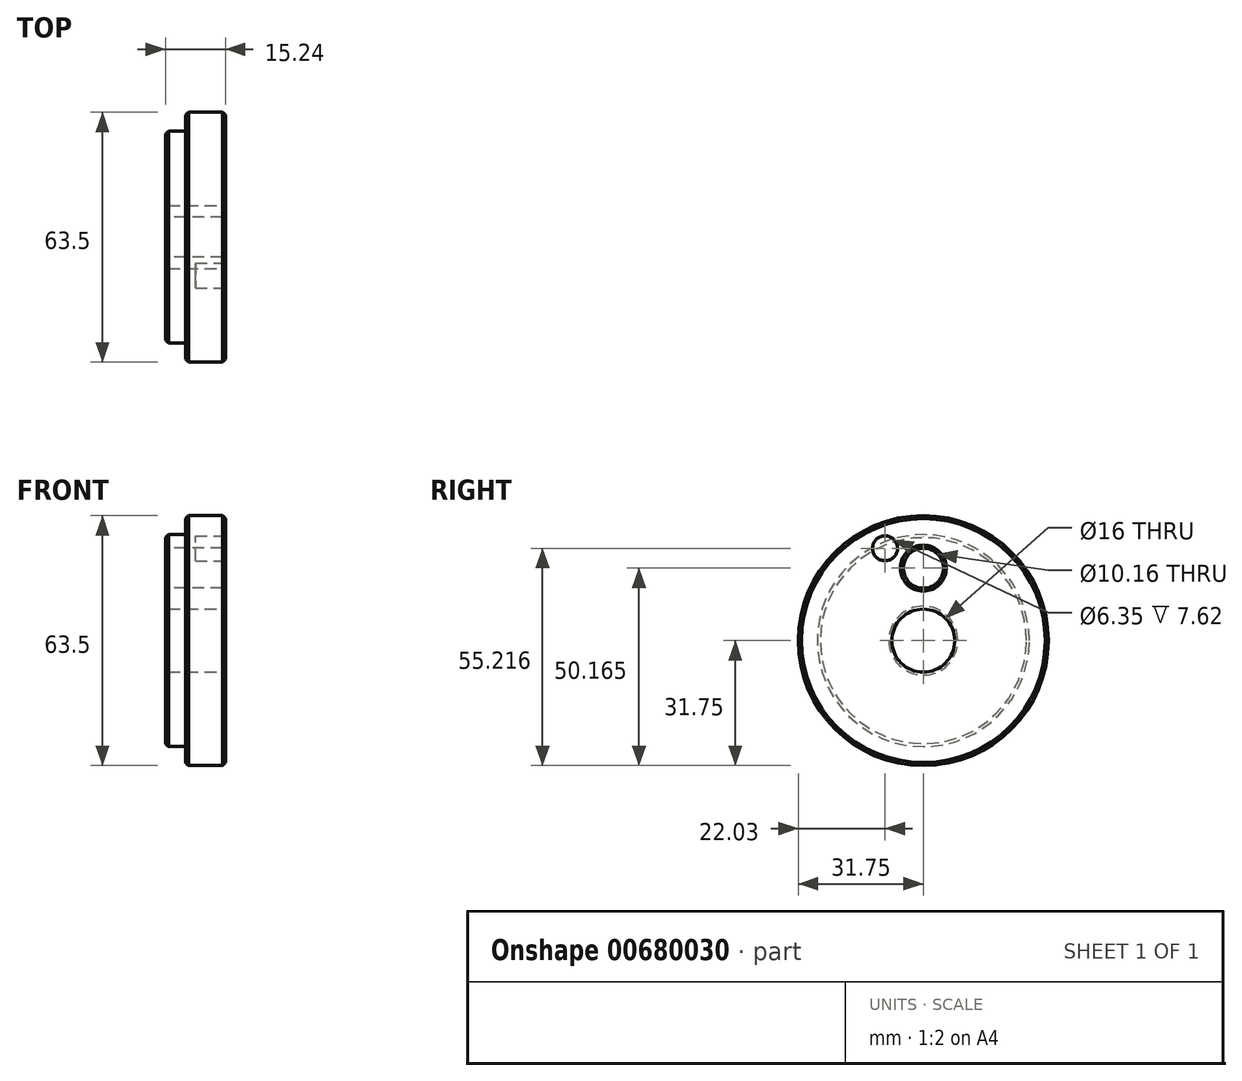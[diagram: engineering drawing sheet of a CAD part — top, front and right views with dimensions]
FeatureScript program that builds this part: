
annotation { "Feature Type Name" : "Feature", "Feature Type Description" : "" }
export const myFeature = defineFeature(function(context is Context, id is Id, definition is map)
    precondition{}
    {
        {
            var Q0;
            Q0=qCreatedBy(makeId("Right.planeOp"),FACE);
            var sketch = newSketch(context, id + "F0", { "sketchPlane" : qUnion([Q0])});
            skCircle(sketch, "E0", {"center": v(0, 0) * mm, "radius": 26.92 * mm});
            skSolve(sketch);
        }
        {
            var Q0;
            Q0 = qSketchRegion(id + "F0", true);
            extrude(context, id + "F1", {"entities" : qUnion([Q0]), "oppositeDirection" : true, "depth" : 5.08 * mm, "offsetDistance" : 25.4 * mm});
        }
        {
            var Q0;
            Q0=makeQuery(id+"F1.opExtrude","CAP_FACE",FACE,{"disambiguationData":[OSD([sQuery(id+"F0.wireOp",EDGE,"E0")])],"isStart":true});
            var sketch = newSketch(context, id + "F2", { "sketchPlane" : qUnion([Q0])});
            skCircle(sketch, "E1", {"center": v(0, 0) * mm, "radius": 31.75 * mm});
            skSolve(sketch);
        }
        {
            var Q0;
            Q0 = qSketchRegion(id + "F2", true);
            extrude(context, id + "F3", {"entities" : qUnion([Q0]), "operationType" : NewBodyOperationType.ADD, "depth" : 10.16 * mm, "offsetDistance" : 25.4 * mm});
        }
        {
            var Q0;
            Q0=makeQuery(id+"F3.opExtrude","CAP_FACE",FACE,{"disambiguationData":[OSD([sQuery(id+"F2.wireOp",EDGE,"E1")])],"isStart":false});
            var sketch = newSketch(context, id + "F4", { "sketchPlane" : qUnion([Q0])});
            skCircle(sketch, "E2", {"center": v(0, 0) * mm, "radius": 8 * mm});
            skSolve(sketch);
        }
        {
            var Q0;
            Q0 = qSketchRegion(id + "F4", true);
            extrude(context, id + "F5", {"entities" : qUnion([Q0]), "operationType" : NewBodyOperationType.REMOVE, "endBound" : BoundingType.THROUGH_ALL, "oppositeDirection" : true, "depth" : 25.4 * mm, "offsetDistance" : 25.4 * mm});
        }
        {
            var Q0;
            Q0=makeQuery(id+"F5.boolean.opBoolean","COPY",EDGE,{"derivedFrom":makeQuery(id+"F5.opExtrude","CAP_EDGE",EDGE,{"disambiguationData":[OSD([sQuery(id+"F4.wireOp",EDGE,"E2")])],"isStart":true})});
            var Q1;
            Q1=makeQuery(id+"F3.opExtrude","CAP_EDGE",EDGE,{"disambiguationData":[OSD([sQuery(id+"F2.wireOp",EDGE,"E1")])],"isStart":false});
            var Q2;
            Q2=makeQuery(id+"F3.opExtrude","CAP_EDGE",EDGE,{"disambiguationData":[OSD([sQuery(id+"F2.wireOp",EDGE,"E1")])],"isStart":true});
            var Q3;
            Q3=makeQuery(id+"F1.opExtrude","CAP_EDGE",EDGE,{"disambiguationData":[OSD([sQuery(id+"F0.wireOp",EDGE,"E0")])],"isStart":false});
            var Q4;
            Q4=makeQuery(id+"F5.boolean.opBoolean","INTERSECT",EDGE,{"derivedFrom":[makeQuery(id+"F1.opExtrude","CAP_FACE",FACE,{"disambiguationData":[OSD([sQuery(id+"F0.wireOp",EDGE,"E0")])],"isStart":false}),makeQuery(id+"F5.opExtrude","SWEPT_FACE",FACE,{"disambiguationData":[OSD([sQuery(id+"F4.wireOp",EDGE,"E2")])]})]});
            chamfer(context, id + "F6", {"entities" : qUnion([Q0, Q1, Q2, Q3, Q4]), "width" : 0.76 * mm, "tangentPropagation" : true});
        }
        {
            var Q0;
            Q0=makeQuery(id+"F1.opExtrude","CAP_FACE",FACE,{"disambiguationData":[OSD([sQuery(id+"F0.wireOp",EDGE,"E0")])],"isStart":false});
            var sketch = newSketch(context, id + "F7", { "sketchPlane" : qUnion([Q0])});
            skCircle(sketch, "E3", {"center": v(0, 18.41) * mm, "radius": 5.08 * mm});
            skSolve(sketch);
        }
        {
            var Q0;
            Q0 = qSketchRegion(id + "F7", true);
            extrude(context, id + "F8", {"entities" : qUnion([Q0]), "operationType" : NewBodyOperationType.REMOVE, "endBound" : BoundingType.THROUGH_ALL, "oppositeDirection" : true, "depth" : 25.4 * mm, "offsetDistance" : 25.4 * mm});
        }
        {
            var Q0;
            Q0=makeQuery(id+"F3.opExtrude","CAP_FACE",FACE,{"disambiguationData":[OSD([sQuery(id+"F2.wireOp",EDGE,"E1")])],"isStart":false});
            var sketch = newSketch(context, id + "F9", { "sketchPlane" : qUnion([Q0])});
            skLineSegment(sketch, "E4", {"start": v(0, 0) * mm, "end": v(-15.54, 37.52) * mm, "construction": true});
            skCircle(sketch, "E5", {"center": v(-9.72, 23.47) * mm, "radius": 3.17 * mm});
            skSolve(sketch);
        }
        {
            var Q0;
            Q0 = qSketchRegion(id + "F9", true);
            extrude(context, id + "F10", {"entities" : qUnion([Q0]), "operationType" : NewBodyOperationType.REMOVE, "oppositeDirection" : true, "depth" : 7.62 * mm, "offsetDistance" : 25.4 * mm});
        }
        {
            var Q0;
            Q0=makeQuery(id+"F10.boolean.opBoolean","COPY",EDGE,{"derivedFrom":makeQuery(id+"F10.opExtrude","CAP_EDGE",EDGE,{"disambiguationData":[OSD([sQuery(id+"F9.wireOp",EDGE,"E5")])],"isStart":true})});
            var Q1;
            Q1=makeQuery(id+"F0EPad4rgIiXKFZ_1.7.F8.boolean.opBoolean","INTERSECT",EDGE,{"derivedFrom":[makeQuery(id+"F3.opExtrude","CAP_FACE",FACE,{"disambiguationData":[OSD([sQuery(id+"F2.wireOp",EDGE,"E1")])],"isStart":false}),makeQuery(id+"F0EPad4rgIiXKFZ_1.7.F8.opExtrude","SWEPT_FACE",FACE,{"disambiguationData":[OSD([sQuery(id+"F7.wireOp",EDGE,"E3")])]})]});
            var Q2;
            Q2=makeQuery(id+"FaLHAEMCEZgUnTc_1.7.F10.boolean.opBoolean","COPY",EDGE,{"derivedFrom":makeQuery(id+"FaLHAEMCEZgUnTc_1.7.F10.opExtrude","CAP_EDGE",EDGE,{"disambiguationData":[OSD([sQuery(id+"F9.wireOp",EDGE,"E5")])],"isStart":true})});
            var Q3;
            Q3=makeQuery(id+"F0EPad4rgIiXKFZ_1.6.F8.boolean.opBoolean","INTERSECT",EDGE,{"derivedFrom":[makeQuery(id+"F3.opExtrude","CAP_FACE",FACE,{"disambiguationData":[OSD([sQuery(id+"F2.wireOp",EDGE,"E1")])],"isStart":false}),makeQuery(id+"F0EPad4rgIiXKFZ_1.6.F8.opExtrude","SWEPT_FACE",FACE,{"disambiguationData":[OSD([sQuery(id+"F7.wireOp",EDGE,"E3")])]})]});
            var Q4;
            Q4=makeQuery(id+"FaLHAEMCEZgUnTc_1.6.F10.boolean.opBoolean","COPY",EDGE,{"derivedFrom":makeQuery(id+"FaLHAEMCEZgUnTc_1.6.F10.opExtrude","CAP_EDGE",EDGE,{"disambiguationData":[OSD([sQuery(id+"F9.wireOp",EDGE,"E5")])],"isStart":true})});
            var Q5;
            Q5=makeQuery(id+"F0EPad4rgIiXKFZ_1.5.F8.boolean.opBoolean","INTERSECT",EDGE,{"derivedFrom":[makeQuery(id+"F3.opExtrude","CAP_FACE",FACE,{"disambiguationData":[OSD([sQuery(id+"F2.wireOp",EDGE,"E1")])],"isStart":false}),makeQuery(id+"F0EPad4rgIiXKFZ_1.5.F8.opExtrude","SWEPT_FACE",FACE,{"disambiguationData":[OSD([sQuery(id+"F7.wireOp",EDGE,"E3")])]})]});
            var Q6;
            Q6=makeQuery(id+"FaLHAEMCEZgUnTc_1.5.F10.boolean.opBoolean","COPY",EDGE,{"derivedFrom":makeQuery(id+"FaLHAEMCEZgUnTc_1.5.F10.opExtrude","CAP_EDGE",EDGE,{"disambiguationData":[OSD([sQuery(id+"F9.wireOp",EDGE,"E5")])],"isStart":true})});
            var Q7;
            Q7=makeQuery(id+"F0EPad4rgIiXKFZ_1.4.F8.boolean.opBoolean","INTERSECT",EDGE,{"derivedFrom":[makeQuery(id+"F3.opExtrude","CAP_FACE",FACE,{"disambiguationData":[OSD([sQuery(id+"F2.wireOp",EDGE,"E1")])],"isStart":false}),makeQuery(id+"F0EPad4rgIiXKFZ_1.4.F8.opExtrude","SWEPT_FACE",FACE,{"disambiguationData":[OSD([sQuery(id+"F7.wireOp",EDGE,"E3")])]})]});
            var Q8;
            Q8=makeQuery(id+"FaLHAEMCEZgUnTc_1.4.F10.boolean.opBoolean","COPY",EDGE,{"derivedFrom":makeQuery(id+"FaLHAEMCEZgUnTc_1.4.F10.opExtrude","CAP_EDGE",EDGE,{"disambiguationData":[OSD([sQuery(id+"F9.wireOp",EDGE,"E5")])],"isStart":true})});
            var Q9;
            Q9=makeQuery(id+"F0EPad4rgIiXKFZ_1.3.F8.boolean.opBoolean","INTERSECT",EDGE,{"derivedFrom":[makeQuery(id+"F3.opExtrude","CAP_FACE",FACE,{"disambiguationData":[OSD([sQuery(id+"F2.wireOp",EDGE,"E1")])],"isStart":false}),makeQuery(id+"F0EPad4rgIiXKFZ_1.3.F8.opExtrude","SWEPT_FACE",FACE,{"disambiguationData":[OSD([sQuery(id+"F7.wireOp",EDGE,"E3")])]})]});
            var Q10;
            Q10=makeQuery(id+"FaLHAEMCEZgUnTc_1.3.F10.boolean.opBoolean","COPY",EDGE,{"derivedFrom":makeQuery(id+"FaLHAEMCEZgUnTc_1.3.F10.opExtrude","CAP_EDGE",EDGE,{"disambiguationData":[OSD([sQuery(id+"F9.wireOp",EDGE,"E5")])],"isStart":true})});
            var Q11;
            Q11=makeQuery(id+"F0EPad4rgIiXKFZ_1.2.F8.boolean.opBoolean","INTERSECT",EDGE,{"derivedFrom":[makeQuery(id+"F3.opExtrude","CAP_FACE",FACE,{"disambiguationData":[OSD([sQuery(id+"F2.wireOp",EDGE,"E1")])],"isStart":false}),makeQuery(id+"F0EPad4rgIiXKFZ_1.2.F8.opExtrude","SWEPT_FACE",FACE,{"disambiguationData":[OSD([sQuery(id+"F7.wireOp",EDGE,"E3")])]})]});
            var Q12;
            Q12=makeQuery(id+"FaLHAEMCEZgUnTc_1.2.F10.boolean.opBoolean","COPY",EDGE,{"derivedFrom":makeQuery(id+"FaLHAEMCEZgUnTc_1.2.F10.opExtrude","CAP_EDGE",EDGE,{"disambiguationData":[OSD([sQuery(id+"F9.wireOp",EDGE,"E5")])],"isStart":true})});
            var Q13;
            Q13=makeQuery(id+"F0EPad4rgIiXKFZ_1.1.F8.boolean.opBoolean","INTERSECT",EDGE,{"derivedFrom":[makeQuery(id+"F3.opExtrude","CAP_FACE",FACE,{"disambiguationData":[OSD([sQuery(id+"F2.wireOp",EDGE,"E1")])],"isStart":false}),makeQuery(id+"F0EPad4rgIiXKFZ_1.1.F8.opExtrude","SWEPT_FACE",FACE,{"disambiguationData":[OSD([sQuery(id+"F7.wireOp",EDGE,"E3")])]})]});
            var Q14;
            Q14=makeQuery(id+"FaLHAEMCEZgUnTc_1.1.F10.boolean.opBoolean","COPY",EDGE,{"derivedFrom":makeQuery(id+"FaLHAEMCEZgUnTc_1.1.F10.opExtrude","CAP_EDGE",EDGE,{"disambiguationData":[OSD([sQuery(id+"F9.wireOp",EDGE,"E5")])],"isStart":true})});
            var Q15;
            Q15=makeQuery(id+"F8.boolean.opBoolean","INTERSECT",EDGE,{"derivedFrom":[makeQuery(id+"F3.opExtrude","CAP_FACE",FACE,{"disambiguationData":[OSD([sQuery(id+"F2.wireOp",EDGE,"E1")])],"isStart":false}),makeQuery(id+"F8.opExtrude","SWEPT_FACE",FACE,{"disambiguationData":[OSD([sQuery(id+"F7.wireOp",EDGE,"E3")])]})]});
            var Q16;
            Q16=makeQuery(id+"F8.boolean.opBoolean","COPY",EDGE,{"derivedFrom":makeQuery(id+"F8.opExtrude","CAP_EDGE",EDGE,{"disambiguationData":[OSD([sQuery(id+"F7.wireOp",EDGE,"E3")])],"isStart":true})});
            var Q17;
            Q17=makeQuery(id+"F0EPad4rgIiXKFZ_1.1.F8.boolean.opBoolean","COPY",EDGE,{"derivedFrom":makeQuery(id+"F0EPad4rgIiXKFZ_1.1.F8.opExtrude","CAP_EDGE",EDGE,{"disambiguationData":[OSD([sQuery(id+"F7.wireOp",EDGE,"E3")])],"isStart":true})});
            var Q18;
            Q18=makeQuery(id+"F0EPad4rgIiXKFZ_1.2.F8.boolean.opBoolean","COPY",EDGE,{"derivedFrom":makeQuery(id+"F0EPad4rgIiXKFZ_1.2.F8.opExtrude","CAP_EDGE",EDGE,{"disambiguationData":[OSD([sQuery(id+"F7.wireOp",EDGE,"E3")])],"isStart":true})});
            var Q19;
            Q19=makeQuery(id+"F0EPad4rgIiXKFZ_1.3.F8.boolean.opBoolean","COPY",EDGE,{"derivedFrom":makeQuery(id+"F0EPad4rgIiXKFZ_1.3.F8.opExtrude","CAP_EDGE",EDGE,{"disambiguationData":[OSD([sQuery(id+"F7.wireOp",EDGE,"E3")])],"isStart":true})});
            var Q20;
            Q20=makeQuery(id+"F0EPad4rgIiXKFZ_1.4.F8.boolean.opBoolean","COPY",EDGE,{"derivedFrom":makeQuery(id+"F0EPad4rgIiXKFZ_1.4.F8.opExtrude","CAP_EDGE",EDGE,{"disambiguationData":[OSD([sQuery(id+"F7.wireOp",EDGE,"E3")])],"isStart":true})});
            var Q21;
            Q21=makeQuery(id+"F0EPad4rgIiXKFZ_1.5.F8.boolean.opBoolean","COPY",EDGE,{"derivedFrom":makeQuery(id+"F0EPad4rgIiXKFZ_1.5.F8.opExtrude","CAP_EDGE",EDGE,{"disambiguationData":[OSD([sQuery(id+"F7.wireOp",EDGE,"E3")])],"isStart":true})});
            var Q22;
            Q22=makeQuery(id+"F0EPad4rgIiXKFZ_1.6.F8.boolean.opBoolean","COPY",EDGE,{"derivedFrom":makeQuery(id+"F0EPad4rgIiXKFZ_1.6.F8.opExtrude","CAP_EDGE",EDGE,{"disambiguationData":[OSD([sQuery(id+"F7.wireOp",EDGE,"E3")])],"isStart":true})});
            var Q23;
            Q23=makeQuery(id+"F0EPad4rgIiXKFZ_1.7.F8.boolean.opBoolean","COPY",EDGE,{"derivedFrom":makeQuery(id+"F0EPad4rgIiXKFZ_1.7.F8.opExtrude","CAP_EDGE",EDGE,{"disambiguationData":[OSD([sQuery(id+"F7.wireOp",EDGE,"E3")])],"isStart":true})});
            chamfer(context, id + "F11", {"entities" : qUnion([Q0, Q1, Q2, Q3, Q4, Q5, Q6, Q7, Q8, Q9, Q10, Q11, Q12, Q13, Q14, Q15, Q16, Q17, Q18, Q19, Q20, Q21, Q22, Q23]), "width" : 0.76 * mm, "tangentPropagation" : true});
        }
    });
